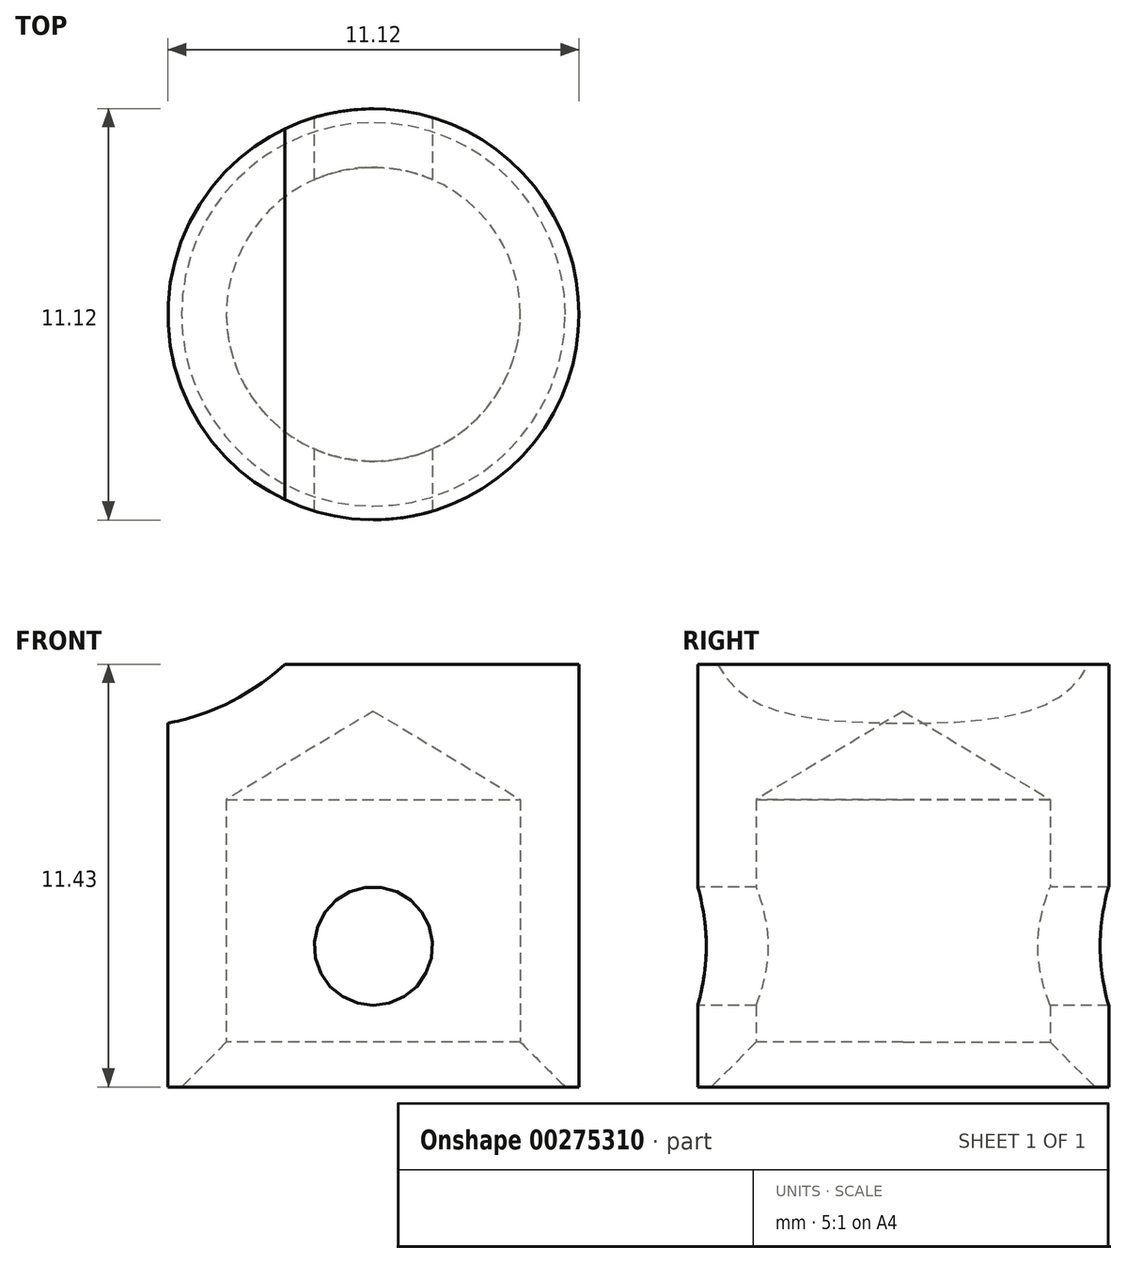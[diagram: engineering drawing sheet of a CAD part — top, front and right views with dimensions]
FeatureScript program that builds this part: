
annotation { "Feature Type Name" : "Feature", "Feature Type Description" : "" }
export const myFeature = defineFeature(function(context is Context, id is Id, definition is map)
    precondition{}
    {
        {
            var Q0;
            Q0=qCreatedBy(makeId("Top.planeOp"),FACE);
            var sketch = newSketch(context, id + "F0", { "sketchPlane" : qUnion([Q0])});
            skCircle(sketch, "E0", {"center": v(0, 0) * mm, "radius": 5.56 * mm});
            skSolve(sketch);
        }
        {
            var Q0;
            Q0 = qSketchRegion(id + "F0", true);
            extrude(context, id + "F1", {"entities" : qUnion([Q0]), "depth" : 11.43 * mm});
        }
        {
            var Q0;
            Q0=makeQuery(id+"F1.opExtrude","CAP_FACE",FACE,{"disambiguationData":[OSD([sQuery(id+"F0.wireOp",EDGE,"E0")])],"isStart":true});
            var sketch = newSketch(context, id + "F2", { "sketchPlane" : qUnion([Q0])});
            skPoint(sketch, "E1", {"position": v(0, 0) * mm});
            skSolve(sketch);
        }
        {
            var Q0;
            Q0=sQuery(id+"F2.wireOp",VERTEX,"E1");
            var Q1;
            Q1=makeQuery(id+"F1.opExtrude","SWEPT_BODY",BODY,{"disambiguationData":[OSD([sQuery(id+"F0.wireOp",EDGE,"E0")])]});
            hole(context, id + "F3", {"style" : HoleStyle.SIMPLE, "endStyle" : HoleEndStyle.BLIND, "holeDiameter" : 7.95 * mm, "holeDepth" : 7.77 * mm, "tappedDepth" : 12.7 * mm, "tapClearance" : 3, "locations" : qUnion([Q0]), "scope" : qUnion([Q1])});
        }
        {
            var Q0;
            Q0=qCreatedBy(makeId("Front.planeOp"),FACE);
            var sketch = newSketch(context, id + "F4", { "sketchPlane" : qUnion([Q0])});
            skLineSegment(sketch, "E2", {"start": v(5.56, 11.43) * mm, "end": v(-5.56, 11.43) * mm, "construction": true});
            skLineSegment(sketch, "E3", {"start": v(5.56, 11.43) * mm, "end": v(5.56, 0) * mm, "construction": true});
            skLineSegment(sketch, "E4", {"start": v(-5.56, 0) * mm, "end": v(-5.56, 11.43) * mm, "construction": true});
            skLineSegment(sketch, "E5", {"start": v(3.98, 7.77) * mm, "end": v(3.98, 0) * mm, "construction": true});
            skLineSegment(sketch, "E6", {"start": v(-3.98, 0) * mm, "end": v(-3.98, 7.77) * mm, "construction": true});
            skCircle(sketch, "E7", {"center": v(-6.72, 16.08) * mm, "radius": 6.35 * mm});
            skLineSegment(sketch, "E8", {"start": v(0, 11.43) * mm, "end": v(0, 0) * mm, "construction": true});
            skCircle(sketch, "E9", {"center": v(0, 3.81) * mm, "radius": 1.6 * mm, "construction": true});
            skLineSegment(sketch, "E10", {"start": v(-5.18, 0) * mm, "end": v(-3.98, 0) * mm, "construction": true});
            skLineSegment(sketch, "E11", {"start": v(-3.98, 1.2) * mm, "end": v(-5.18, 0) * mm, "construction": true});
            skLineSegment(sketch, "E12", {"start": v(-3.98, 1.2) * mm, "end": v(-6.76, 1.2) * mm, "construction": true});
            skSolve(sketch);
        }
        {
            var Q0;
            Q0=makeQuery(id+"F4.imprint","IMPRINT",FACE,{"disambiguationData":[TD([[makeQuery(id+"F4.imprint","IMPRINT",EDGE,{"derivedFrom":sQuery(id+"F4.wireOp",EDGE,"E7")}),1.0]])]});
            extrude(context, id + "F5", {"entities" : qUnion([Q0]), "operationType" : NewBodyOperationType.REMOVE, "endBound" : BoundingType.SYMMETRIC, "oppositeDirection" : true, "depth" : 25.4 * mm});
        }
        {
            var Q0;
            Q0=qCreatedBy(makeId("Front.planeOp"),FACE);
            var sketch = newSketch(context, id + "F6", { "sketchPlane" : qUnion([Q0])});
            skCircle(sketch, "E13.0", {"center": v(0, 3.81) * mm, "radius": 1.6 * mm});
            skSolve(sketch);
        }
        {
            var Q0;
            Q0 = qSketchRegion(id + "F6", true);
            extrude(context, id + "F7", {"entities" : qUnion([Q0]), "operationType" : NewBodyOperationType.REMOVE, "endBound" : BoundingType.SYMMETRIC, "oppositeDirection" : true, "depth" : 25.4 * mm});
        }
        {
            var Q0;
            Q0=qCreatedBy(makeId("Front.planeOp"),FACE);
            var sketch = newSketch(context, id + "F8", { "sketchPlane" : qUnion([Q0])});
            skLineSegment(sketch, "E14.0", {"start": v(-3.98, 1.2) * mm, "end": v(-5.18, 0) * mm});
            skLineSegment(sketch, "E15.0", {"start": v(-5.18, 0) * mm, "end": v(-3.98, 0) * mm});
            skLineSegment(sketch, "E16", {"start": v(-3.98, 1.2) * mm, "end": v(-3.98, 0) * mm});
            skLineSegment(sketch, "E17", {"start": v(0, 0) * mm, "end": v(0, 13.12) * mm, "construction": true});
            skSolve(sketch);
        }
        {
            var Q0;
            Q0 = qSketchRegion(id + "F8", true);
            var Q1;
            Q1=sQuery(id+"F8.wireOp",EDGE,"E17");
            revolve(context, id + "F9", {"operationType" : NewBodyOperationType.REMOVE, "entities" : qUnion([Q0]), "axis" : qUnion([Q1]), "revolveType" : RevolveType.FULL, "oppositeDirection" : true});
        }
    });
